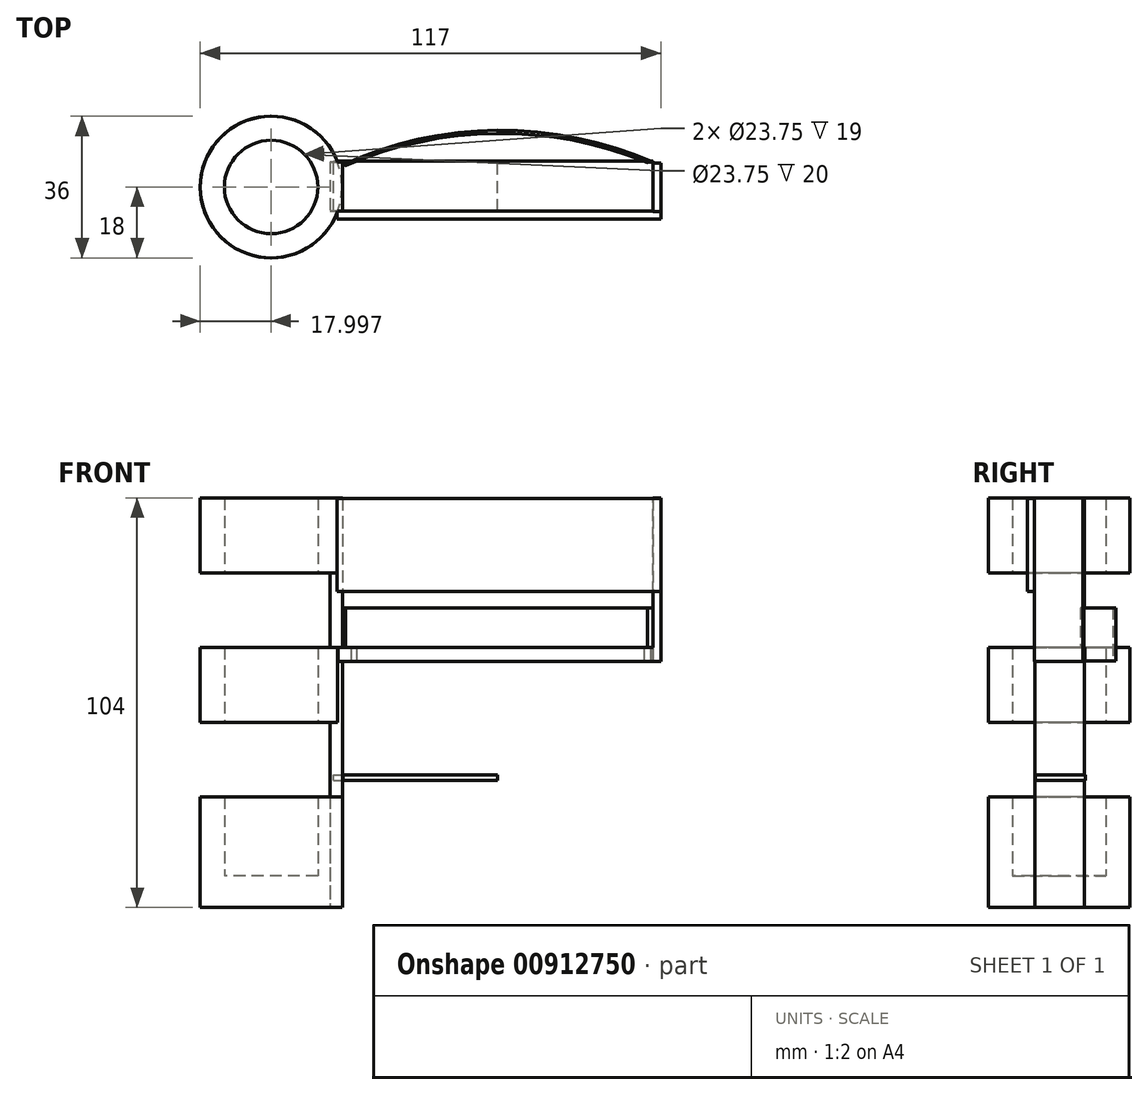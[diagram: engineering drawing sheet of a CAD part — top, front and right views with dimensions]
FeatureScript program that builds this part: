
annotation { "Feature Type Name" : "Feature", "Feature Type Description" : "" }
export const myFeature = defineFeature(function(context is Context, id is Id, definition is map)
    precondition{}
    {
        {
            var Q0;
            Q0=qCreatedBy(makeId("Top.planeOp"),FACE);
            var sketch = newSketch(context, id + "F0", { "sketchPlane" : qUnion([Q0])});
            skCircle(sketch, "E0", {"center": v(-64.56, 2.48) * mm, "radius": 18 * mm});
            skSolve(sketch);
        }
        {
            var Q0;
            Q0 = qSketchRegion(id + "F0", true);
            extrude(context, id + "F1", {"entities" : qUnion([Q0]), "depth" : 8 * mm, "offsetDistance" : 25 * mm});
        }
        {
            var Q0;
            Q0=makeQuery(id+"F1.opExtrude","CAP_FACE",FACE,{"disambiguationData":[OSD([sQuery(id+"F0.wireOp",EDGE,"E0")])],"isStart":false});
            var sketch = newSketch(context, id + "F2", { "sketchPlane" : qUnion([Q0])});
            skCircle(sketch, "E1", {"center": v(-64.56, 2.48) * mm, "radius": 11.88 * mm});
            skSolve(sketch);
        }
        {
            var Q0;
            Q0=makeQuery(id+"F2.imprint","IMPRINT",FACE,{"disambiguationData":[TD([[makeQuery(id+"F2.imprint","IMPRINT",EDGE,{"derivedFrom":sQuery(id+"F2.wireOp",EDGE,"E1")}),-1.0]])]});
            extrude(context, id + "F3", {"entities" : qUnion([Q0]), "operationType" : NewBodyOperationType.ADD, "depth" : 96 * mm, "offsetDistance" : 25 * mm});
        }
        {
            var Q0;
            Q0=makeQuery(id+"F3.opExtrude","CAP_FACE",FACE,{"disambiguationData":[OSD([sQuery(id+"F0.wireOp",EDGE,"E0"),sQuery(id+"F2.wireOp",EDGE,"E1")])],"isStart":false});
            cPlane(context, id + "F4", {"entities" : qUnion([Q0]), "cplaneType" : CPlaneType.OFFSET, "offset" : 19 * mm, "oppositeDirection" : true, "width" : 150 * mm, "height" : 150 * mm});
        }
        {
            var Q0;
            Q0=qCreatedBy(id+"F4.planeOp",FACE);
            cPlane(context, id + "F5", {"entities" : qUnion([Q0]), "cplaneType" : CPlaneType.OFFSET, "offset" : 19 * mm, "oppositeDirection" : true, "width" : 150 * mm, "height" : 150 * mm});
        }
        {
            var Q0;
            Q0=qCreatedBy(id+"F5.planeOp",FACE);
            cPlane(context, id + "F6", {"entities" : qUnion([Q0]), "cplaneType" : CPlaneType.OFFSET, "offset" : 19 * mm, "oppositeDirection" : true, "width" : 150 * mm, "height" : 150 * mm});
        }
        {
            var Q0;
            Q0=qCreatedBy(id+"F5.planeOp",FACE);
            var sketch = newSketch(context, id + "F7", { "sketchPlane" : qUnion([Q0])});
            skLineSegment(sketch, "E2.bottom", {"start": v(-117.1, -27.67) * mm, "end": v(-2.84, -27.67) * mm});
            skLineSegment(sketch, "E2.top", {"start": v(-117.1, 43.37) * mm, "end": v(-2.84, 43.37) * mm});
            skLineSegment(sketch, "E2.left", {"start": v(-117.1, -27.67) * mm, "end": v(-117.1, 43.37) * mm});
            skLineSegment(sketch, "E2.right", {"start": v(-2.84, -27.67) * mm, "end": v(-2.84, 43.37) * mm});
            skSolve(sketch);
        }
        {
            var Q0;
            Q0 = qSketchRegion(id + "F7", true);
            extrude(context, id + "F8", {"entities" : qUnion([Q0]), "operationType" : NewBodyOperationType.REMOVE, "depth" : 19 * mm, "offsetDistance" : 25 * mm});
        }
        {
            var Q0;
            Q0=qCreatedBy(id+"F6.planeOp",FACE);
            var sketch = newSketch(context, id + "F9", { "sketchPlane" : qUnion([Q0])});
            skLineSegment(sketch, "E3.bottom", {"start": v(-134.77, -40.96) * mm, "end": v(8.12, -40.96) * mm});
            skLineSegment(sketch, "E3.top", {"start": v(-134.77, 48.4) * mm, "end": v(8.12, 48.4) * mm});
            skLineSegment(sketch, "E3.left", {"start": v(-134.77, -40.96) * mm, "end": v(-134.77, 48.4) * mm});
            skLineSegment(sketch, "E3.right", {"start": v(8.12, -40.96) * mm, "end": v(8.12, 48.4) * mm});
            skSolve(sketch);
        }
        {
            var Q0;
            Q0 = qSketchRegion(id + "F9", true);
            extrude(context, id + "F10", {"entities" : qUnion([Q0]), "operationType" : NewBodyOperationType.REMOVE, "oppositeDirection" : true, "depth" : 19 * mm, "offsetDistance" : 25 * mm});
        }
        {
            var Q0;
            Q0=qCreatedBy(makeId("Top.planeOp"),FACE);
            var sketch = newSketch(context, id + "F11", { "sketchPlane" : qUnion([Q0])});
            skLineSegment(sketch, "E4.bottom", {"start": v(-47.03, 8.87) * mm, "end": v(-50.03, 8.87) * mm});
            skLineSegment(sketch, "E4.top", {"start": v(-47.03, -3.63) * mm, "end": v(-50.03, -3.63) * mm});
            skLineSegment(sketch, "E5.bottom", {"start": v(-49.55, -3.63) * mm, "end": v(-46.43, -3.63) * mm});
            skLineSegment(sketch, "E5.top", {"start": v(-49.55, 8.87) * mm, "end": v(-46.43, 8.87) * mm});
            skLineSegment(sketch, "E5.left", {"start": v(-49.55, -3.63) * mm, "end": v(-49.55, 8.87) * mm});
            skLineSegment(sketch, "E5.right", {"start": v(-46.43, -3.63) * mm, "end": v(-46.43, 8.87) * mm});
            skSolve(sketch);
        }
        {
            var Q0;
            Q0 = qSketchRegion(id + "F11", true);
            extrude(context, id + "F12", {"entities" : qUnion([Q0]), "depth" : 104 * mm, "offsetDistance" : 25 * mm});
        }
        {
            var Q0;
            Q0=makeQuery(id+"F3.opExtrude","CAP_FACE",FACE,{"disambiguationData":[OSD([sQuery(id+"F0.wireOp",EDGE,"E0"),sQuery(id+"F2.wireOp",EDGE,"E1")])],"isStart":false});
            cPlane(context, id + "F13", {"entities" : qUnion([Q0]), "cplaneType" : CPlaneType.OFFSET, "offset" : 38 * mm, "oppositeDirection" : true, "width" : 150 * mm, "height" : 150 * mm});
        }
        {
            var Q0;
            Q0=qCreatedBy(id+"F13.planeOp",FACE);
            var sketch = newSketch(context, id + "F14", { "sketchPlane" : qUnion([Q0])});
            skLineSegment(sketch, "E6.bottom", {"start": v(-47.56, -3.77) * mm, "end": v(32.44, -3.77) * mm});
            skLineSegment(sketch, "E6.top", {"start": v(-47.56, 9.06) * mm, "end": v(32.44, 9.06) * mm});
            skLineSegment(sketch, "E6.left", {"start": v(-47.56, -3.77) * mm, "end": v(-47.56, 9.06) * mm});
            skLineSegment(sketch, "E6.right", {"start": v(32.44, -3.77) * mm, "end": v(32.44, 9.06) * mm});
            skSolve(sketch);
        }
        {
            var Q0;
            Q0 = qSketchRegion(id + "F14", true);
            extrude(context, id + "F15", {"entities" : qUnion([Q0]), "operationType" : NewBodyOperationType.ADD, "oppositeDirection" : true, "depth" : 3.5 * mm, "offsetDistance" : 25 * mm});
        }
        {
            var Q0;
            Q0=makeQuery(id+"F15.opExtrude","SWEPT_FACE",FACE,{"disambiguationData":[OSD([sQuery(id+"F14.wireOp",EDGE,"E6.right")])]});
            var sketch = newSketch(context, id + "F16", { "sketchPlane" : qUnion([Q0])});
            skLineSegment(sketch, "E7.bottom", {"start": v(-3.77, 62.5) * mm, "end": v(8.53, 62.5) * mm});
            skLineSegment(sketch, "E7.top", {"start": v(-3.77, 104) * mm, "end": v(8.53, 104) * mm});
            skLineSegment(sketch, "E7.left", {"start": v(-3.77, 62.5) * mm, "end": v(-3.77, 104) * mm});
            skLineSegment(sketch, "E7.right", {"start": v(8.53, 62.5) * mm, "end": v(8.53, 104) * mm});
            skSolve(sketch);
        }
        {
            var Q0;
            {var subQ0=sQuery(id+"F16.wireOp",EDGE,"E7.top");Q0=makeQuery(id+"F16.imprint","IMPRINT",FACE,{"disambiguationData":[TD([[makeQuery(id+"F16.imprint","IMPRINT",EDGE,{"derivedFrom":subQ0}),-1.0]])]});}
            var Q1;
            {var subQ0=sQuery(id+"F16.wireOp",EDGE,"E7.bottom");Q1=makeQuery(id+"F16.imprint","IMPRINT",FACE,{"disambiguationData":[TD([[makeQuery(id+"F16.imprint","IMPRINT",EDGE,{"derivedFrom":subQ0}),1.0]])]});}
            extrude(context, id + "F17", {"entities" : qUnion([Q0, Q1]), "operationType" : NewBodyOperationType.ADD, "depth" : 2 * mm, "offsetDistance" : 25 * mm});
        }
        {
            var Q0;
            Q0=makeQuery(id+"F12.opExtrude","SWEPT_FACE",FACE,{"disambiguationData":[OSD([sQuery(id+"F11.wireOp",EDGE,"E5.bottom")])]});
            var sketch = newSketch(context, id + "F18", { "sketchPlane" : qUnion([Q0])});
            skLineSegment(sketch, "E8.bottom", {"start": v(-47.77, 80.27) * mm, "end": v(34.43, 80.27) * mm});
            skLineSegment(sketch, "E8.top", {"start": v(-47.77, 103.88) * mm, "end": v(34.43, 103.88) * mm});
            skLineSegment(sketch, "E8.left", {"start": v(-47.77, 80.27) * mm, "end": v(-47.77, 103.88) * mm});
            skLineSegment(sketch, "E8.right", {"start": v(34.43, 80.27) * mm, "end": v(34.43, 103.88) * mm});
            skSolve(sketch);
        }
        {
            var Q0;
            Q0 = qSketchRegion(id + "F18", true);
            extrude(context, id + "F19", {"entities" : qUnion([Q0]), "operationType" : NewBodyOperationType.ADD, "depth" : 2 * mm, "offsetDistance" : 25 * mm});
        }
        {
            var Q0;
            Q0=qCreatedBy(makeId("Top.planeOp"),FACE);
            cPlane(context, id + "F20", {"entities" : qUnion([Q0]), "cplaneType" : CPlaneType.OFFSET, "offset" : 62.6 * mm, "width" : 150 * mm, "height" : 150 * mm});
        }
        {
            var Q0;
            Q0=qCreatedBy(id+"F20.planeOp",FACE);
            var sketch = newSketch(context, id + "F21", { "sketchPlane" : qUnion([Q0])});
            skArc(sketch, "E9", {"start": v(32.5, 8.77) * mm, "mid": v(-7.15, 16.88) * mm, "end": v(-46.63, 8.01) * mm});
            skArc(sketch, "E10", {"start": v(31.06, 8.73) * mm, "mid": v(-7.35, 16.1) * mm, "end": v(-45.6, 7.94) * mm});
            skLineSegment(sketch, "E11", {"start": v(-46.63, 8.01) * mm, "end": v(-45.6, 7.94) * mm});
            skLineSegment(sketch, "E12", {"start": v(31.06, 8.73) * mm, "end": v(32.5, 8.77) * mm});
            skLineSegment(sketch, "E13", {"start": v(32.5, 8.77) * mm, "end": v(34.01, 8.1) * mm});
            skLineSegment(sketch, "E14", {"start": v(34.01, 8.1) * mm, "end": v(34.01, 7.49) * mm});
            skLineSegment(sketch, "E15", {"start": v(34.01, 7.49) * mm, "end": v(33.25, 7.49) * mm});
            skLineSegment(sketch, "E16", {"start": v(33.25, 7.49) * mm, "end": v(32.5, 8.23) * mm});
            skLineSegment(sketch, "E17", {"start": v(32.5, 8.23) * mm, "end": v(31.06, 8.73) * mm});
            skSolve(sketch);
        }
        {
            var Q0;
            Q0=makeQuery(id+"F21.imprint","IMPRINT",FACE,{"disambiguationData":[TD([[makeQuery(id+"F21.imprint","IMPRINT",EDGE,{"derivedFrom":sQuery(id+"F21.wireOp",EDGE,"E9")}),1.0]])]});
            extrude(context, id + "F22", {"entities" : qUnion([Q0]), "operationType" : NewBodyOperationType.ADD, "depth" : 13.5 * mm, "offsetDistance" : 25 * mm});
        }
        {
            var Q0;
            Q0=qCreatedBy(id+"F20.planeOp",FACE);
            cPlane(context, id + "F23", {"entities" : qUnion([Q0]), "cplaneType" : CPlaneType.OFFSET, "offset" : 29 * mm, "oppositeDirection" : true, "width" : 150 * mm, "height" : 150 * mm});
        }
        {
            var Q0;
            Q0=qCreatedBy(id+"F23.planeOp",FACE);
            var sketch = newSketch(context, id + "F24", { "sketchPlane" : qUnion([Q0])});
            skLineSegment(sketch, "E18.bottom", {"start": v(-46.27, -3.6) * mm, "end": v(-6.98, -3.6) * mm});
            skLineSegment(sketch, "E18.top", {"start": v(-46.27, 9.1) * mm, "end": v(-6.98, 9.1) * mm});
            skLineSegment(sketch, "E18.left", {"start": v(-46.27, -3.6) * mm, "end": v(-46.27, 9.1) * mm});
            skLineSegment(sketch, "E18.right", {"start": v(-6.98, -3.6) * mm, "end": v(-6.98, 9.1) * mm});
            skSolve(sketch);
        }
        {
            var Q0;
            Q0 = qSketchRegion(id + "F24", true);
            extrude(context, id + "F25", {"entities" : qUnion([Q0]), "oppositeDirection" : true, "depth" : 1.3 * mm, "offsetDistance" : 25 * mm});
        }
        {
            var Q0;
            Q0=makeQuery(id+"F25.opExtrude","SWEPT_FACE",FACE,{"disambiguationData":[OSD([sQuery(id+"F24.wireOp",EDGE,"E18.left")])]});
            extrude(context, id + "F26", {"entities" : qUnion([Q0]), "depth" : 2.4 * mm, "offsetDistance" : 25 * mm});
        }
    });
